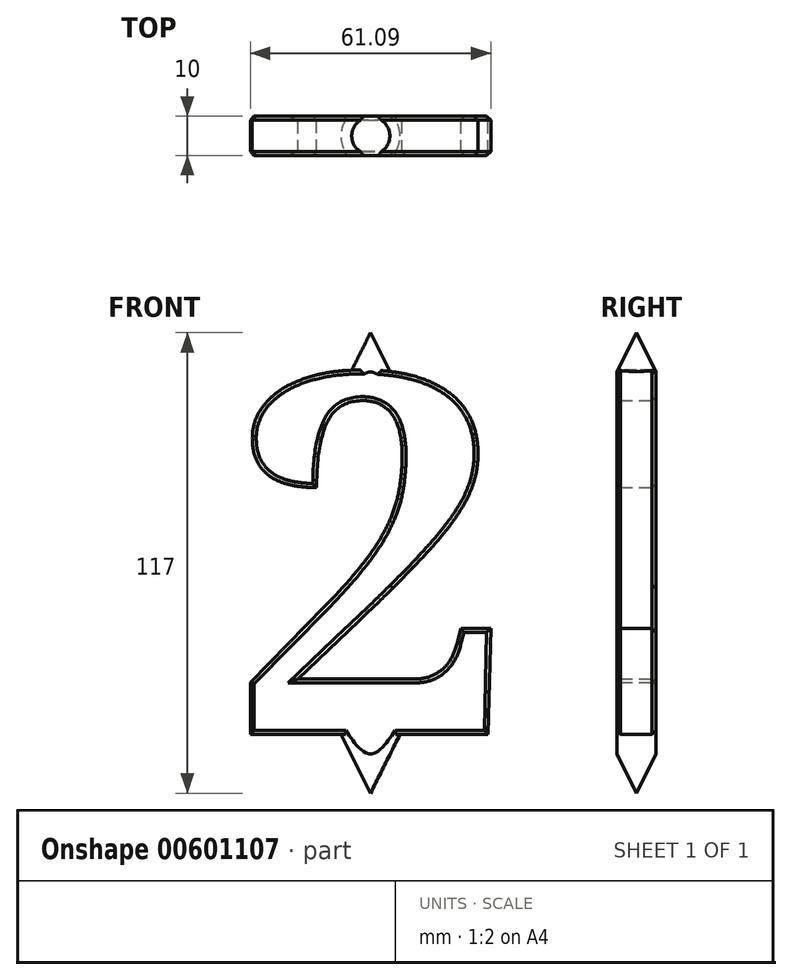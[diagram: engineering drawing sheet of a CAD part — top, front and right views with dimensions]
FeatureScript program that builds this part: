
annotation { "Feature Type Name" : "Feature", "Feature Type Description" : "" }
export const myFeature = defineFeature(function(context is Context, id is Id, definition is map)
    precondition{}
    {
        {
            var Q0;
            Q0=qCreatedBy(makeId("Front.planeOp"),FACE);
            var sketch = newSketch(context, id + "F0", { "sketchPlane" : qUnion([Q0])});
            skLineSegment(sketch, "E0", {"start": v(0, 108.8) * mm, "end": v(0, -162.25) * mm, "construction": true});
            skPoint(sketch, "E1", {"position": v(0, 0) * mm});
            skCircle(sketch, "E2", {"center": v(0, 0) * mm, "radius": 55 * mm});
            skCircle(sketch, "E3", {"center": v(0, 0) * mm, "radius": 60 * mm});
            skCircle(sketch, "E4", {"center": v(0, 0) * mm, "radius": 65 * mm});
            skArc(sketch, "E5", {"start": v(-32.84, -61.82) * mm, "mid": v(0, -70) * mm, "end": v(32.84, -61.82) * mm});
            skLineSegment(sketch, "E6", {"start": v(0, 58.5) * mm, "end": v(-3, 54.92) * mm});
            skLineSegment(sketch, "E7.MirrorCS", {"start": v(0, 58.5) * mm, "end": v(3, 54.92) * mm});
            skLineSegment(sketch, "E8.MirrorCS", {"start": v(0, -58.5) * mm, "end": v(3, -54.92) * mm});
            skLineSegment(sketch, "E9.MirrorCS", {"start": v(0, -58.5) * mm, "end": v(-3, -54.92) * mm});
            skLineSegment(sketch, "E10", {"start": v(-68.5, 0) * mm, "end": v(-64.93, 3) * mm});
            skLineSegment(sketch, "E11", {"start": v(-87.59, 0) * mm, "end": v(84.79, 0) * mm, "construction": true});
            skLineSegment(sketch, "E12", {"start": v(-68.5, 0) * mm, "end": v(-59.87, 4) * mm});
            skLineSegment(sketch, "E13.MirrorCS", {"start": v(-68.5, 0) * mm, "end": v(-64.93, -3) * mm});
            skLineSegment(sketch, "E14.MirrorCS", {"start": v(-68.5, 0) * mm, "end": v(-59.87, -4) * mm});
            skLineSegment(sketch, "E15.MirrorCS", {"start": v(68.5, 0) * mm, "end": v(59.87, -4) * mm});
            skLineSegment(sketch, "E16.MirrorCS", {"start": v(68.5, 0) * mm, "end": v(64.93, -3) * mm});
            skLineSegment(sketch, "E17.MirrorCS", {"start": v(68.5, 0) * mm, "end": v(64.93, 3) * mm});
            skLineSegment(sketch, "E18.MirrorCS", {"start": v(68.5, 0) * mm, "end": v(59.87, 4) * mm});
            skArc(sketch, "E19", {"start": v(-20.47, -232.01) * mm, "mid": v(-7.18, -135.51) * mm, "end": v(-50.64, -48.33) * mm});
            skArc(sketch, "E20", {"start": v(-66.54, -290.79) * mm, "mid": v(-5.35, -173.05) * mm, "end": v(-50.64, -48.33) * mm});
            skLineSegment(sketch, "E21", {"start": v(-70, 0) * mm, "end": v(-70, -493.69) * mm, "construction": true});
            skLineSegment(sketch, "E22", {"start": v(-70, -299.76) * mm, "end": v(0, -299.76) * mm});
            skLineSegment(sketch, "E23", {"start": v(-70, -299.76) * mm, "end": v(-66.54, -290.79) * mm});
            skArc(sketch, "E24.trimOffspring", {"start": v(-70, -299.73) * mm, "mid": v(-2.04, -188.49) * mm, "end": v(-32.84, -61.82) * mm});
            skLineSegment(sketch, "E25.trimOffspring", {"start": v(0, -299.76) * mm, "end": v(0, -400) * mm, "construction": true});
            skLineSegment(sketch, "E26.MirrorCS", {"start": v(70, -299.76) * mm, "end": v(66.54, -290.79) * mm});
            skLineSegment(sketch, "E27.MirrorCS", {"start": v(70, -299.76) * mm, "end": v(0, -299.76) * mm});
            skArc(sketch, "E28.MirrorCS", {"start": v(70, -299.73) * mm, "mid": v(2.04, -188.49) * mm, "end": v(32.84, -61.82) * mm});
            skArc(sketch, "E29.MirrorCS", {"start": v(66.54, -290.79) * mm, "mid": v(5.35, -173.05) * mm, "end": v(50.64, -48.33) * mm});
            skArc(sketch, "E30.trimOffspring", {"start": v(50.64, -48.33) * mm, "mid": v(0, 70) * mm, "end": v(-50.64, -48.33) * mm});
            skLineSegment(sketch, "E31.bottom", {"start": v(-70, -299.73) * mm, "end": v(70, -299.73) * mm});
            skLineSegment(sketch, "E31.top", {"start": v(-70, -304.73) * mm, "end": v(70, -304.73) * mm});
            skLineSegment(sketch, "E31.left", {"start": v(-70, -299.73) * mm, "end": v(-70, -304.73) * mm});
            skLineSegment(sketch, "E31.right", {"start": v(70, -299.73) * mm, "end": v(70, -304.73) * mm});
            skLineSegment(sketch, "E32", {"start": v(-59.87, 0) * mm, "end": v(-59.87, -4) * mm});
            skLineSegment(sketch, "E33", {"start": v(59.87, 4) * mm, "end": v(59.87, 0) * mm});
            skLineSegment(sketch, "E34", {"start": v(-59.87, 0) * mm, "end": v(-68.5, 0) * mm});
            skLineSegment(sketch, "E35", {"start": v(-53.44, -232.25) * mm, "end": v(49.45, -232.25) * mm, "construction": true});
            skLineSegment(sketch, "E36", {"start": v(0, -299.76) * mm, "end": v(0, -162.25) * mm, "construction": true});
            skLineSegment(sketch, "E37", {"start": v(0, -232.25) * mm, "end": v(-5, -232.25) * mm});
            skLineSegment(sketch, "E38", {"start": v(-5, -222.25) * mm, "end": v(-5, -232.25) * mm});
            skLineSegment(sketch, "E39", {"start": v(-5, -222.25) * mm, "end": v(-16.3, -222.25) * mm});
            skLineSegment(sketch, "E40.MirrorCS", {"start": v(5, -222.25) * mm, "end": v(5, -232.25) * mm});
            skLineSegment(sketch, "E41.MirrorCS", {"start": v(5, -222.25) * mm, "end": v(16.3, -222.25) * mm});
            skLineSegment(sketch, "E42", {"start": v(-5, -232.25) * mm, "end": v(5, -232.25) * mm});
            skLineSegment(sketch, "E43", {"start": v(-64.93, -3) * mm, "end": v(-64.93, 0) * mm});
            skLineSegment(sketch, "E44", {"start": v(-64.93, 0) * mm, "end": v(-68.5, 0) * mm});
            skLineSegment(sketch, "E45", {"start": v(64.93, -3) * mm, "end": v(64.93, 0) * mm});
            skLineSegment(sketch, "E46", {"start": v(64.93, 0) * mm, "end": v(68.5, 0) * mm});
            skLineSegment(sketch, "E47", {"start": v(-70, -299.73) * mm, "end": v(-70, -179.73) * mm});
            skLineSegment(sketch, "E48", {"start": v(-70, -179.73) * mm, "end": v(0, -179.73) * mm});
            skArc(sketch, "E49", {"start": v(0, -232.65) * mm, "mid": v(-16.4, -263.54) * mm, "end": v(-38.33, -290.78) * mm});
            skArc(sketch, "E50.MirrorCS", {"start": v(0, -232.65) * mm, "mid": v(16.4, -263.54) * mm, "end": v(38.33, -290.78) * mm});
            skLineSegment(sketch, "E51", {"start": v(-38.33, -290.78) * mm, "end": v(38.33, -290.78) * mm});
            skSolve(sketch);
        }
        {
            var Q0;
            Q0=qCreatedBy(makeId("Front.planeOp"),FACE);
            var sketch = newSketch(context, id + "F1", { "sketchPlane" : qUnion([Q0])});
            skText(sketch, "E52", { "text": "2", "fontName": "NotoSerif-Bold.ttf"});
            const initialGuessF1  = {"E52": [-0.03892, -0.0434, 1, 0, 0.09202]};
            skSetInitialGuess(sketch, initialGuessF1);
            skSolve(sketch);
        }
        {
            var Q0;
            Q0=qCreatedBy(makeId("Front.planeOp"),FACE);
            var sketch = newSketch(context, id + "F2", { "sketchPlane" : qUnion([Q0])});
            skPoint(sketch, "E53.0", {"position": v(0, -58.5) * mm});
            skPoint(sketch, "E54.0", {"position": v(0, 58.5) * mm});
            skLineSegment(sketch, "E55", {"start": v(0, 58.5) * mm, "end": v(-6.97, 44.58) * mm});
            skLineSegment(sketch, "E56", {"start": v(0, 44.58) * mm, "end": v(0, 58.5) * mm});
            skLineSegment(sketch, "E57", {"start": v(0, -58.5) * mm, "end": v(-6.46, -45.6) * mm});
            skLineSegment(sketch, "E58", {"start": v(-6.46, -45.6) * mm, "end": v(-8.12, -42.3) * mm});
            skLineSegment(sketch, "E59", {"start": v(0, -58.5) * mm, "end": v(0, -42.3) * mm});
            skLineSegment(sketch, "E60", {"start": v(0, 44.58) * mm, "end": v(-4.93, 44.58) * mm});
            skLineSegment(sketch, "E61", {"start": v(0, -42.3) * mm, "end": v(-7.6, -42.3) * mm});
            skPoint(sketch, "E62.end.orphan", {"position": v(-8, 42.54) * mm});
            skPoint(sketch, "E63.orphan", {"position": v(0, 42.54) * mm});
            skPoint(sketch, "E64.orphan", {"position": v(0, -39.54) * mm});
            skLineSegment(sketch, "E65", {"start": v(-6.97, 44.58) * mm, "end": v(-4.93, 44.58) * mm});
            skLineSegment(sketch, "E66", {"start": v(-8.12, -42.3) * mm, "end": v(-7.6, -42.3) * mm});
            skPoint(sketch, "E67.end.orphan", {"position": v(-7.6, -42.8) * mm});
            skPoint(sketch, "E67.start.orphan", {"position": v(-7.6, -43.31) * mm});
            skSolve(sketch);
        }
        {
            var Q0;
            Q0=qSketchRegion(id+"F1",true);
            extrude(context, id + "F3", {"entities" : qUnion([Q0]), "endBound" : BoundingType.SYMMETRIC, "depth" : 10 * mm, "offsetDistance" : 25 * mm});
        }
        {
            var Q0;
            Q0=makeQuery(id+"F3.opExtrude","SWEPT_BODY",BODY,{"disambiguationData":[OSD([sQuery(id+"F1.wireOp",EDGE,"E52.sketch_text.stroke-0"),sQuery(id+"F1.wireOp",EDGE,"E52.sketch_text.stroke-1"),sQuery(id+"F1.wireOp",EDGE,"E52.sketch_text.stroke-2"),sQuery(id+"F1.wireOp",EDGE,"E52.sketch_text.stroke-3"),sQuery(id+"F1.wireOp",EDGE,"E52.sketch_text.stroke-4"),sQuery(id+"F1.wireOp",EDGE,"E52.sketch_text.stroke-5"),sQuery(id+"F1.wireOp",EDGE,"E52.sketch_text.stroke-6"),sQuery(id+"F1.wireOp",EDGE,"E52.sketch_text.stroke-7"),sQuery(id+"F1.wireOp",EDGE,"E52.sketch_text.stroke-8"),sQuery(id+"F1.wireOp",EDGE,"E52.sketch_text.stroke-9"),sQuery(id+"F1.wireOp",EDGE,"E52.sketch_text.stroke-10"),sQuery(id+"F1.wireOp",EDGE,"E52.sketch_text.stroke-11"),sQuery(id+"F1.wireOp",EDGE,"E52.sketch_text.stroke-12"),sQuery(id+"F1.wireOp",EDGE,"E52.sketch_text.stroke-13"),sQuery(id+"F1.wireOp",EDGE,"E52.sketch_text.stroke-14"),sQuery(id+"F1.wireOp",EDGE,"E52.sketch_text.stroke-15"),sQuery(id+"F1.wireOp",EDGE,"E52.sketch_text.stroke-16"),sQuery(id+"F1.wireOp",EDGE,"E52.sketch_text.stroke-17"),sQuery(id+"F1.wireOp",EDGE,"E52.sketch_text.stroke-18"),sQuery(id+"F1.wireOp",EDGE,"E52.sketch_text.stroke-19"),sQuery(id+"F1.wireOp",EDGE,"E52.sketch_text.stroke-20"),sQuery(id+"F1.wireOp",EDGE,"E52.sketch_text.stroke-21"),sQuery(id+"F1.wireOp",EDGE,"E52.sketch_text.stroke-22"),sQuery(id+"F1.wireOp",EDGE,"E52.sketch_text.stroke-23"),sQuery(id+"F1.wireOp",EDGE,"E52.sketch_text.stroke-24"),sQuery(id+"F1.wireOp",EDGE,"E52.sketch_text.stroke-25"),sQuery(id+"F1.wireOp",EDGE,"E52.sketch_text.stroke-26"),sQuery(id+"F1.wireOp",EDGE,"E52.sketch_text.stroke-27"),sQuery(id+"F1.wireOp",EDGE,"E52.sketch_text.stroke-28")])]});
            transform(context, id + "F4", {"entities" : qUnion([Q0]), "transformType" : TransformType.TRANSLATION_3D, "dx" : 3.9 * mm, "dy" : 0 * mm, "dz" : -0.1 * mm, "makeCopy" : false});
        }
        {
            var Q0;
            Q0=makeQuery(id+"F3.opExtrude","CAP_FACE",FACE,{"disambiguationData":[OSD([sQuery(id+"F1.wireOp",EDGE,"E52.sketch_text.stroke-0"),sQuery(id+"F1.wireOp",EDGE,"E52.sketch_text.stroke-1"),sQuery(id+"F1.wireOp",EDGE,"E52.sketch_text.stroke-2"),sQuery(id+"F1.wireOp",EDGE,"E52.sketch_text.stroke-3"),sQuery(id+"F1.wireOp",EDGE,"E52.sketch_text.stroke-4"),sQuery(id+"F1.wireOp",EDGE,"E52.sketch_text.stroke-5"),sQuery(id+"F1.wireOp",EDGE,"E52.sketch_text.stroke-6"),sQuery(id+"F1.wireOp",EDGE,"E52.sketch_text.stroke-7"),sQuery(id+"F1.wireOp",EDGE,"E52.sketch_text.stroke-8"),sQuery(id+"F1.wireOp",EDGE,"E52.sketch_text.stroke-9"),sQuery(id+"F1.wireOp",EDGE,"E52.sketch_text.stroke-10"),sQuery(id+"F1.wireOp",EDGE,"E52.sketch_text.stroke-11"),sQuery(id+"F1.wireOp",EDGE,"E52.sketch_text.stroke-12"),sQuery(id+"F1.wireOp",EDGE,"E52.sketch_text.stroke-13"),sQuery(id+"F1.wireOp",EDGE,"E52.sketch_text.stroke-14"),sQuery(id+"F1.wireOp",EDGE,"E52.sketch_text.stroke-15"),sQuery(id+"F1.wireOp",EDGE,"E52.sketch_text.stroke-16"),sQuery(id+"F1.wireOp",EDGE,"E52.sketch_text.stroke-17"),sQuery(id+"F1.wireOp",EDGE,"E52.sketch_text.stroke-18"),sQuery(id+"F1.wireOp",EDGE,"E52.sketch_text.stroke-19"),sQuery(id+"F1.wireOp",EDGE,"E52.sketch_text.stroke-20"),sQuery(id+"F1.wireOp",EDGE,"E52.sketch_text.stroke-21"),sQuery(id+"F1.wireOp",EDGE,"E52.sketch_text.stroke-22"),sQuery(id+"F1.wireOp",EDGE,"E52.sketch_text.stroke-23"),sQuery(id+"F1.wireOp",EDGE,"E52.sketch_text.stroke-24"),sQuery(id+"F1.wireOp",EDGE,"E52.sketch_text.stroke-25"),sQuery(id+"F1.wireOp",EDGE,"E52.sketch_text.stroke-26"),sQuery(id+"F1.wireOp",EDGE,"E52.sketch_text.stroke-27"),sQuery(id+"F1.wireOp",EDGE,"E52.sketch_text.stroke-28")])],"isStart":false});
            var Q1;
            Q1=makeQuery(id+"F3.opExtrude","CAP_FACE",FACE,{"disambiguationData":[OSD([sQuery(id+"F1.wireOp",EDGE,"E52.sketch_text.stroke-0"),sQuery(id+"F1.wireOp",EDGE,"E52.sketch_text.stroke-1"),sQuery(id+"F1.wireOp",EDGE,"E52.sketch_text.stroke-2"),sQuery(id+"F1.wireOp",EDGE,"E52.sketch_text.stroke-3"),sQuery(id+"F1.wireOp",EDGE,"E52.sketch_text.stroke-4"),sQuery(id+"F1.wireOp",EDGE,"E52.sketch_text.stroke-5"),sQuery(id+"F1.wireOp",EDGE,"E52.sketch_text.stroke-6"),sQuery(id+"F1.wireOp",EDGE,"E52.sketch_text.stroke-7"),sQuery(id+"F1.wireOp",EDGE,"E52.sketch_text.stroke-8"),sQuery(id+"F1.wireOp",EDGE,"E52.sketch_text.stroke-9"),sQuery(id+"F1.wireOp",EDGE,"E52.sketch_text.stroke-10"),sQuery(id+"F1.wireOp",EDGE,"E52.sketch_text.stroke-11"),sQuery(id+"F1.wireOp",EDGE,"E52.sketch_text.stroke-12"),sQuery(id+"F1.wireOp",EDGE,"E52.sketch_text.stroke-13"),sQuery(id+"F1.wireOp",EDGE,"E52.sketch_text.stroke-14"),sQuery(id+"F1.wireOp",EDGE,"E52.sketch_text.stroke-15"),sQuery(id+"F1.wireOp",EDGE,"E52.sketch_text.stroke-16"),sQuery(id+"F1.wireOp",EDGE,"E52.sketch_text.stroke-17"),sQuery(id+"F1.wireOp",EDGE,"E52.sketch_text.stroke-18"),sQuery(id+"F1.wireOp",EDGE,"E52.sketch_text.stroke-19"),sQuery(id+"F1.wireOp",EDGE,"E52.sketch_text.stroke-20"),sQuery(id+"F1.wireOp",EDGE,"E52.sketch_text.stroke-21"),sQuery(id+"F1.wireOp",EDGE,"E52.sketch_text.stroke-22"),sQuery(id+"F1.wireOp",EDGE,"E52.sketch_text.stroke-23"),sQuery(id+"F1.wireOp",EDGE,"E52.sketch_text.stroke-24"),sQuery(id+"F1.wireOp",EDGE,"E52.sketch_text.stroke-25"),sQuery(id+"F1.wireOp",EDGE,"E52.sketch_text.stroke-26"),sQuery(id+"F1.wireOp",EDGE,"E52.sketch_text.stroke-27"),sQuery(id+"F1.wireOp",EDGE,"E52.sketch_text.stroke-28")])],"isStart":true});
            chamfer(context, id + "F5", {"entities" : qUnion([Q0, Q1]), "width" : 1 * mm, "tangentPropagation" : true});
        }
        {
            var Q0;
            Q0=makeQuery(id+"F2.imprint","IMPRINT",FACE,{"disambiguationData":[TD([[makeQuery(id+"F2.imprint","IMPRINT",EDGE,{"derivedFrom":sQuery(id+"F2.wireOp",EDGE,"E55")}),1.0]])]});
            var Q1;
            Q1=makeQuery(id+"F2.imprint","IMPRINT",FACE,{"disambiguationData":[TD([[makeQuery(id+"F2.imprint","IMPRINT",EDGE,{"derivedFrom":sQuery(id+"F2.wireOp",EDGE,"E57")}),-1.0]])]});
            var Q2;
            Q2=sQuery(id+"F0.wireOp",EDGE,"E0");
            revolve(context, id + "F6", {"operationType" : NewBodyOperationType.ADD, "entities" : qUnion([Q0, Q1]), "axis" : qUnion([Q2]), "revolveType" : RevolveType.FULL});
        }
        {
            var Q0;
            Q0=makeQuery(id+"F3.opExtrude","CAP_FACE",FACE,{"disambiguationData":[OSD([sQuery(id+"F1.wireOp",EDGE,"E52.sketch_text.stroke-0"),sQuery(id+"F1.wireOp",EDGE,"E52.sketch_text.stroke-1"),sQuery(id+"F1.wireOp",EDGE,"E52.sketch_text.stroke-2"),sQuery(id+"F1.wireOp",EDGE,"E52.sketch_text.stroke-3"),sQuery(id+"F1.wireOp",EDGE,"E52.sketch_text.stroke-4"),sQuery(id+"F1.wireOp",EDGE,"E52.sketch_text.stroke-5"),sQuery(id+"F1.wireOp",EDGE,"E52.sketch_text.stroke-6"),sQuery(id+"F1.wireOp",EDGE,"E52.sketch_text.stroke-7"),sQuery(id+"F1.wireOp",EDGE,"E52.sketch_text.stroke-8"),sQuery(id+"F1.wireOp",EDGE,"E52.sketch_text.stroke-9"),sQuery(id+"F1.wireOp",EDGE,"E52.sketch_text.stroke-10"),sQuery(id+"F1.wireOp",EDGE,"E52.sketch_text.stroke-11"),sQuery(id+"F1.wireOp",EDGE,"E52.sketch_text.stroke-12"),sQuery(id+"F1.wireOp",EDGE,"E52.sketch_text.stroke-13"),sQuery(id+"F1.wireOp",EDGE,"E52.sketch_text.stroke-14"),sQuery(id+"F1.wireOp",EDGE,"E52.sketch_text.stroke-15"),sQuery(id+"F1.wireOp",EDGE,"E52.sketch_text.stroke-16"),sQuery(id+"F1.wireOp",EDGE,"E52.sketch_text.stroke-17"),sQuery(id+"F1.wireOp",EDGE,"E52.sketch_text.stroke-18"),sQuery(id+"F1.wireOp",EDGE,"E52.sketch_text.stroke-19"),sQuery(id+"F1.wireOp",EDGE,"E52.sketch_text.stroke-20"),sQuery(id+"F1.wireOp",EDGE,"E52.sketch_text.stroke-21"),sQuery(id+"F1.wireOp",EDGE,"E52.sketch_text.stroke-22"),sQuery(id+"F1.wireOp",EDGE,"E52.sketch_text.stroke-23"),sQuery(id+"F1.wireOp",EDGE,"E52.sketch_text.stroke-24"),sQuery(id+"F1.wireOp",EDGE,"E52.sketch_text.stroke-25"),sQuery(id+"F1.wireOp",EDGE,"E52.sketch_text.stroke-26"),sQuery(id+"F1.wireOp",EDGE,"E52.sketch_text.stroke-27"),sQuery(id+"F1.wireOp",EDGE,"E52.sketch_text.stroke-28")])],"isStart":false});
            var sketch = newSketch(context, id + "F7", { "sketchPlane" : qUnion([Q0])});
            skPoint(sketch, "E68.0", {"position": v(-38.92, 48.62) * mm});
            skPoint(sketch, "E69.0", {"position": v(34.94, -43.4) * mm});
            skLineSegment(sketch, "E70.left", {"start": v(-38.92, 48.62) * mm, "end": v(-38.92, -43.4) * mm});
            skLineSegment(sketch, "E70.right", {"start": v(34.94, 48.62) * mm, "end": v(34.94, -43.4) * mm});
            skLineSegment(sketch, "E71.top", {"start": v(-38.92, -58.8) * mm, "end": v(34.94, -58.8) * mm});
            skLineSegment(sketch, "E71.left", {"start": v(-38.92, -43.4) * mm, "end": v(-38.92, -58.8) * mm});
            skLineSegment(sketch, "E71.right", {"start": v(34.94, -43.4) * mm, "end": v(34.94, -58.8) * mm});
            skLineSegment(sketch, "E72.top", {"start": v(-38.92, 62.38) * mm, "end": v(34.94, 62.38) * mm});
            skLineSegment(sketch, "E72.left", {"start": v(-38.92, 48.62) * mm, "end": v(-38.92, 62.38) * mm});
            skLineSegment(sketch, "E72.right", {"start": v(34.94, 48.62) * mm, "end": v(34.94, 62.38) * mm});
            skLineSegment(sketch, "E73.left", {"start": v(-38.92, 62.38) * mm, "end": v(-38.92, -58.8) * mm});
            skLineSegment(sketch, "E73.right", {"start": v(34.94, 62.38) * mm, "end": v(34.94, -58.8) * mm});
            skSolve(sketch);
        }
        {
            var Q0;
            {var subQ50=sQuery(id+"F7.wireOp",EDGE,"E72.top");Q0=makeQuery(id+"F7.imprint","IMPRINT",FACE,{"disambiguationData":[TD([[makeQuery(id+"F7.imprint","IMPRINT",EDGE,{"derivedFrom":subQ50}),-1.0]])]});}
            var Q1;
            {var subQ0=sQuery(id+"F1.wireOp",EDGE,"E52.sketch_text.stroke-35");var subQ1=sQuery(id+"F1.wireOp",EDGE,"E52.sketch_text.stroke-34");var subQ2=sQuery(id+"F1.wireOp",EDGE,"E52.sketch_text.stroke-33");var subQ3=sQuery(id+"F1.wireOp",EDGE,"E52.sketch_text.stroke-32");var subQ4=sQuery(id+"F1.wireOp",EDGE,"E52.sketch_text.stroke-31");var subQ5=sQuery(id+"F1.wireOp",EDGE,"E52.sketch_text.stroke-30");var subQ6=sQuery(id+"F1.wireOp",EDGE,"E52.sketch_text.stroke-29");var subQ7=sQuery(id+"F1.wireOp",EDGE,"E52.sketch_text.stroke-28");var subQ8=sQuery(id+"F1.wireOp",EDGE,"E52.sketch_text.stroke-27");var subQ9=sQuery(id+"F1.wireOp",EDGE,"E52.sketch_text.stroke-26");var subQ10=sQuery(id+"F1.wireOp",EDGE,"E52.sketch_text.stroke-25");var subQ11=sQuery(id+"F1.wireOp",EDGE,"E52.sketch_text.stroke-24");var subQ12=sQuery(id+"F1.wireOp",EDGE,"E52.sketch_text.stroke-23");var subQ13=sQuery(id+"F1.wireOp",EDGE,"E52.sketch_text.stroke-22");var subQ14=sQuery(id+"F1.wireOp",EDGE,"E52.sketch_text.stroke-21");var subQ15=sQuery(id+"F1.wireOp",EDGE,"E52.sketch_text.stroke-20");var subQ16=sQuery(id+"F1.wireOp",EDGE,"E52.sketch_text.stroke-19");var subQ17=sQuery(id+"F1.wireOp",EDGE,"E52.sketch_text.stroke-18");var subQ18=sQuery(id+"F1.wireOp",EDGE,"E52.sketch_text.stroke-17");var subQ19=sQuery(id+"F1.wireOp",EDGE,"E52.sketch_text.stroke-16");var subQ20=sQuery(id+"F1.wireOp",EDGE,"E52.sketch_text.stroke-15");var subQ21=sQuery(id+"F1.wireOp",EDGE,"E52.sketch_text.stroke-14");var subQ22=sQuery(id+"F1.wireOp",EDGE,"E52.sketch_text.stroke-13");var subQ23=sQuery(id+"F1.wireOp",EDGE,"E52.sketch_text.stroke-12");var subQ24=sQuery(id+"F1.wireOp",EDGE,"E52.sketch_text.stroke-11");var subQ25=sQuery(id+"F1.wireOp",EDGE,"E52.sketch_text.stroke-10");var subQ26=sQuery(id+"F1.wireOp",EDGE,"E52.sketch_text.stroke-9");var subQ27=sQuery(id+"F1.wireOp",EDGE,"E52.sketch_text.stroke-8");var subQ28=sQuery(id+"F1.wireOp",EDGE,"E52.sketch_text.stroke-7");var subQ29=sQuery(id+"F1.wireOp",EDGE,"E52.sketch_text.stroke-6");var subQ30=sQuery(id+"F1.wireOp",EDGE,"E52.sketch_text.stroke-5");var subQ31=sQuery(id+"F1.wireOp",EDGE,"E52.sketch_text.stroke-4");var subQ32=sQuery(id+"F1.wireOp",EDGE,"E52.sketch_text.stroke-3");var subQ33=sQuery(id+"F1.wireOp",EDGE,"E52.sketch_text.stroke-2");var subQ34=sQuery(id+"F1.wireOp",EDGE,"E52.sketch_text.stroke-1");var subQ35=sQuery(id+"F1.wireOp",EDGE,"E52.sketch_text.stroke-0");var subQ36=makeQuery(id+"F3.opExtrude","CAP_FACE",FACE,{"disambiguationData":[OSD([subQ35,subQ34,subQ33,subQ32,subQ31,subQ30,subQ29,subQ28,subQ27,subQ26,subQ25,subQ24,subQ23,subQ22,subQ21,subQ20,subQ19,subQ18,subQ17,subQ16,subQ15,subQ14,subQ13,subQ12,subQ11,subQ10,subQ9,subQ8,subQ7,subQ6,subQ5,subQ4,subQ3,subQ2,subQ1,subQ0])],"isStart":false});Q1=makeQuery(id+"F7.imprint","IMPRINT",FACE,{"disambiguationData":[TD([[makeQuery(id+"F7.imprint","IMPRINT",EDGE,{"derivedFrom":makeQuery(id+"F5.opChamfer","BLEND_EDGE",EDGE,{"blendedFrom":[makeQuery(id+"F3.opExtrude","CAP_EDGE",EDGE,{"disambiguationData":[OSD([subQ35])],"isStart":false}),subQ36],"blendedInto":[subQ36]})}),1.0]])]});}
            extrude(context, id + "F8", {"entities" : qUnion([Q0, Q1]), "operationType" : NewBodyOperationType.REMOVE, "depth" : 25 * mm, "offsetDistance" : 25 * mm});
        }
        {
            var Q0;
            Q0=makeQuery(id+"F3.opExtrude","CAP_FACE",FACE,{"disambiguationData":[OSD([sQuery(id+"F1.wireOp",EDGE,"E52.sketch_text.stroke-0"),sQuery(id+"F1.wireOp",EDGE,"E52.sketch_text.stroke-1"),sQuery(id+"F1.wireOp",EDGE,"E52.sketch_text.stroke-2"),sQuery(id+"F1.wireOp",EDGE,"E52.sketch_text.stroke-3"),sQuery(id+"F1.wireOp",EDGE,"E52.sketch_text.stroke-4"),sQuery(id+"F1.wireOp",EDGE,"E52.sketch_text.stroke-5"),sQuery(id+"F1.wireOp",EDGE,"E52.sketch_text.stroke-6"),sQuery(id+"F1.wireOp",EDGE,"E52.sketch_text.stroke-7"),sQuery(id+"F1.wireOp",EDGE,"E52.sketch_text.stroke-8"),sQuery(id+"F1.wireOp",EDGE,"E52.sketch_text.stroke-9"),sQuery(id+"F1.wireOp",EDGE,"E52.sketch_text.stroke-10"),sQuery(id+"F1.wireOp",EDGE,"E52.sketch_text.stroke-11"),sQuery(id+"F1.wireOp",EDGE,"E52.sketch_text.stroke-12"),sQuery(id+"F1.wireOp",EDGE,"E52.sketch_text.stroke-13"),sQuery(id+"F1.wireOp",EDGE,"E52.sketch_text.stroke-14"),sQuery(id+"F1.wireOp",EDGE,"E52.sketch_text.stroke-15"),sQuery(id+"F1.wireOp",EDGE,"E52.sketch_text.stroke-16"),sQuery(id+"F1.wireOp",EDGE,"E52.sketch_text.stroke-17"),sQuery(id+"F1.wireOp",EDGE,"E52.sketch_text.stroke-18"),sQuery(id+"F1.wireOp",EDGE,"E52.sketch_text.stroke-19"),sQuery(id+"F1.wireOp",EDGE,"E52.sketch_text.stroke-20"),sQuery(id+"F1.wireOp",EDGE,"E52.sketch_text.stroke-21"),sQuery(id+"F1.wireOp",EDGE,"E52.sketch_text.stroke-22"),sQuery(id+"F1.wireOp",EDGE,"E52.sketch_text.stroke-23"),sQuery(id+"F1.wireOp",EDGE,"E52.sketch_text.stroke-24"),sQuery(id+"F1.wireOp",EDGE,"E52.sketch_text.stroke-25"),sQuery(id+"F1.wireOp",EDGE,"E52.sketch_text.stroke-26"),sQuery(id+"F1.wireOp",EDGE,"E52.sketch_text.stroke-27"),sQuery(id+"F1.wireOp",EDGE,"E52.sketch_text.stroke-28")])],"isStart":true});
            var sketch = newSketch(context, id + "F9", { "sketchPlane" : qUnion([Q0])});
            skLineSegment(sketch, "E74.bottom", {"start": v(-37.22, 63.98) * mm, "end": v(41.68, 63.98) * mm});
            skLineSegment(sketch, "E74.top", {"start": v(-37.22, -58.42) * mm, "end": v(41.68, -58.42) * mm});
            skLineSegment(sketch, "E74.left", {"start": v(-37.22, 63.98) * mm, "end": v(-37.22, -58.42) * mm});
            skLineSegment(sketch, "E74.right", {"start": v(41.68, 63.98) * mm, "end": v(41.68, -58.42) * mm});
            skSolve(sketch);
        }
        {
            var Q0;
            Q0=makeQuery(id+"F9.imprint","IMPRINT",FACE,{"disambiguationData":[TD([[makeQuery(id+"F9.imprint","IMPRINT",EDGE,{"derivedFrom":sQuery(id+"F9.wireOp",EDGE,"E74.bottom")}),-1.0]])]});
            var Q1;
            {var subQ0=sQuery(id+"F1.wireOp",EDGE,"E52.sketch_text.stroke-28");var subQ1=sQuery(id+"F1.wireOp",EDGE,"E52.sketch_text.stroke-27");var subQ2=sQuery(id+"F1.wireOp",EDGE,"E52.sketch_text.stroke-26");var subQ3=sQuery(id+"F1.wireOp",EDGE,"E52.sketch_text.stroke-25");var subQ4=sQuery(id+"F1.wireOp",EDGE,"E52.sketch_text.stroke-24");var subQ5=sQuery(id+"F1.wireOp",EDGE,"E52.sketch_text.stroke-23");var subQ6=sQuery(id+"F1.wireOp",EDGE,"E52.sketch_text.stroke-22");var subQ7=sQuery(id+"F1.wireOp",EDGE,"E52.sketch_text.stroke-21");var subQ8=sQuery(id+"F1.wireOp",EDGE,"E52.sketch_text.stroke-20");var subQ9=sQuery(id+"F1.wireOp",EDGE,"E52.sketch_text.stroke-19");var subQ10=sQuery(id+"F1.wireOp",EDGE,"E52.sketch_text.stroke-18");var subQ11=sQuery(id+"F1.wireOp",EDGE,"E52.sketch_text.stroke-17");var subQ12=sQuery(id+"F1.wireOp",EDGE,"E52.sketch_text.stroke-16");var subQ13=sQuery(id+"F1.wireOp",EDGE,"E52.sketch_text.stroke-15");var subQ14=sQuery(id+"F1.wireOp",EDGE,"E52.sketch_text.stroke-14");var subQ15=sQuery(id+"F1.wireOp",EDGE,"E52.sketch_text.stroke-13");var subQ16=sQuery(id+"F1.wireOp",EDGE,"E52.sketch_text.stroke-12");var subQ17=sQuery(id+"F1.wireOp",EDGE,"E52.sketch_text.stroke-11");var subQ18=sQuery(id+"F1.wireOp",EDGE,"E52.sketch_text.stroke-10");var subQ19=sQuery(id+"F1.wireOp",EDGE,"E52.sketch_text.stroke-9");var subQ20=sQuery(id+"F1.wireOp",EDGE,"E52.sketch_text.stroke-8");var subQ21=sQuery(id+"F1.wireOp",EDGE,"E52.sketch_text.stroke-7");var subQ22=sQuery(id+"F1.wireOp",EDGE,"E52.sketch_text.stroke-6");var subQ23=sQuery(id+"F1.wireOp",EDGE,"E52.sketch_text.stroke-5");var subQ24=sQuery(id+"F1.wireOp",EDGE,"E52.sketch_text.stroke-4");var subQ25=sQuery(id+"F1.wireOp",EDGE,"E52.sketch_text.stroke-3");var subQ26=sQuery(id+"F1.wireOp",EDGE,"E52.sketch_text.stroke-2");var subQ27=sQuery(id+"F1.wireOp",EDGE,"E52.sketch_text.stroke-1");var subQ28=sQuery(id+"F1.wireOp",EDGE,"E52.sketch_text.stroke-0");var subQ29=makeQuery(id+"F3.opExtrude","CAP_FACE",FACE,{"disambiguationData":[OSD([subQ28,subQ27,subQ26,subQ25,subQ24,subQ23,subQ22,subQ21,subQ20,subQ19,subQ18,subQ17,subQ16,subQ15,subQ14,subQ13,subQ12,subQ11,subQ10,subQ9,subQ8,subQ7,subQ6,subQ5,subQ4,subQ3,subQ2,subQ1,subQ0])],"isStart":true});var subQ30=makeQuery(id+"F3.opExtrude","CAP_EDGE",EDGE,{"disambiguationData":[OSD([subQ28])],"isStart":true});Q1=makeQuery(id+"F9.imprint","IMPRINT",FACE,{"disambiguationData":[TD([[makeQuery(id+"F9.imprint","IMPRINT",EDGE,{"derivedFrom":makeQuery(id+"F5.opChamfer","BLEND_EDGE",EDGE,{"blendedFrom":[subQ30,subQ29],"blendedInto":[subQ29]})}),1.0]])]});}
            extrude(context, id + "F10", {"entities" : qUnion([Q0, Q1]), "operationType" : NewBodyOperationType.REMOVE, "depth" : 25 * mm, "offsetDistance" : 25 * mm});
        }
    });
